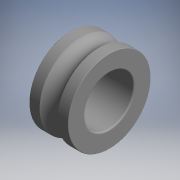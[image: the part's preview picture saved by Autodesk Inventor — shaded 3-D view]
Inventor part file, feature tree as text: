
AUTODESK INVENTOR PART (.ipt)
format: ipt  version: 2017.3 (Build 213256000, 256)  size: 145,408 bytes
history: native  units: mm (DEFAULTED — no unit token found)
features: revolve x1, sketch x1
ambient origin geometry x8: Origin, YZ Plane, XZ Plane, XY Plane, X Axis, Y Axis, Z Axis, Center Point
bodies: Solid1 (feature_tree)
feature tree (2):
  revolve  "Revolution1"  [1 undecoded]
  sketch  "Sketch_54"  dims[d0=360.0deg]
note: 1 required parameter value undecoded (feature->parameter linkage not recoverable at this tier; creation-order binding heuristic only, values carry confidence <= 0.55)
